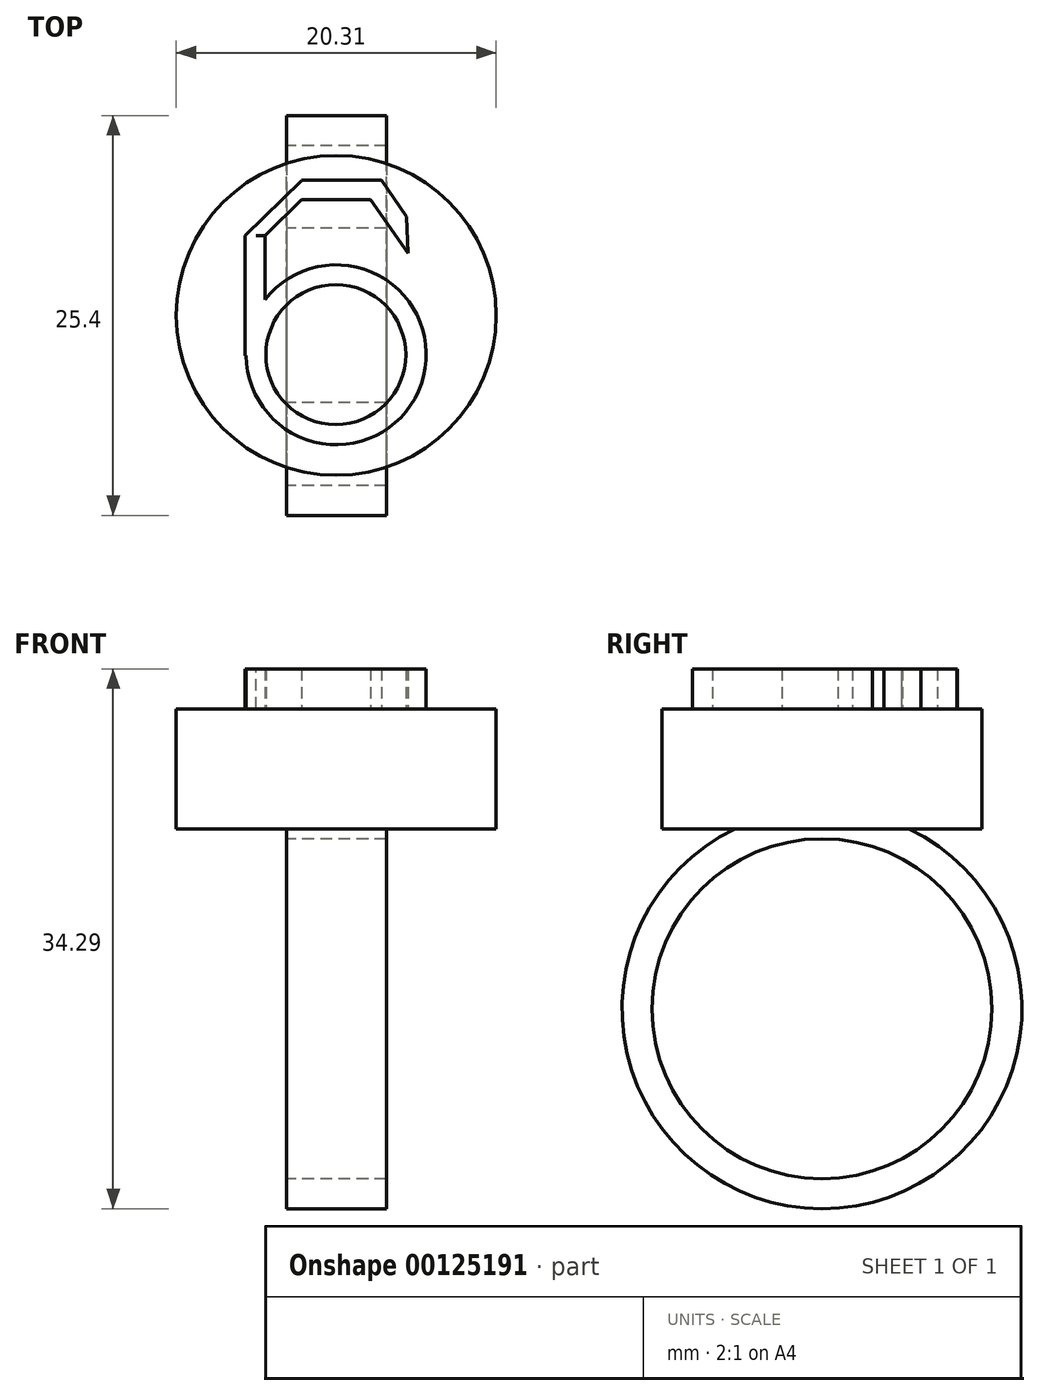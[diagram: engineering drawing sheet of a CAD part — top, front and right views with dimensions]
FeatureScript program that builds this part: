
annotation { "Feature Type Name" : "Feature", "Feature Type Description" : "" }
export const myFeature = defineFeature(function(context is Context, id is Id, definition is map)
    precondition{}
    {
        {
            var Q0;
            Q0=qCreatedBy(makeId("Right.planeOp"),FACE);
            var sketch = newSketch(context, id + "F0", { "sketchPlane" : qUnion([Q0])});
            skCircle(sketch, "E0", {"center": v(0, 0) * mm, "radius": 12.7 * mm});
            skSolve(sketch);
        }
        {
            var Q0;
            Q0 = qSketchRegion(id + "F0", true);
            extrude(context, id + "F1", {"entities" : qUnion([Q0]), "depth" : 6.35 * mm});
        }
        {
            var Q0;
            Q0=qCreatedBy(makeId("Right.planeOp"),FACE);
            var sketch = newSketch(context, id + "F2", { "sketchPlane" : qUnion([Q0])});
            skCircle(sketch, "E1", {"center": v(0, 0) * mm, "radius": 10.8 * mm});
            skSolve(sketch);
        }
        {
            var Q0;
            Q0 = qSketchRegion(id + "F2", true);
            extrude(context, id + "F3", {"entities" : qUnion([Q0]), "operationType" : NewBodyOperationType.REMOVE, "depth" : 55.84 * mm});
        }
        {
            var Q0;
            Q0=qCreatedBy(makeId("Top.planeOp"),FACE);
            cPlane(context, id + "F4", {"entities" : qUnion([Q0]), "cplaneType" : CPlaneType.OFFSET, "offset" : 12.7 * mm, "width" : 152.4 * mm, "height" : 152.4 * mm});
        }
        {
            var Q0;
            Q0=qCreatedBy(id+"F4.planeOp",FACE);
            cPlane(context, id + "F5", {"entities" : qUnion([Q0]), "cplaneType" : CPlaneType.OFFSET, "offset" : 1.27 * mm, "oppositeDirection" : true, "width" : 152.4 * mm, "height" : 152.4 * mm});
        }
        {
            var Q0;
            Q0=qCreatedBy(id+"F5.planeOp",FACE);
            var sketch = newSketch(context, id + "F6", { "sketchPlane" : qUnion([Q0])});
            skCircle(sketch, "E2", {"center": v(3.16, 0) * mm, "radius": 10.16 * mm});
            skSolve(sketch);
        }
        {
            var Q0;
            Q0 = qSketchRegion(id + "F6", true);
            extrude(context, id + "F7", {"entities" : qUnion([Q0]), "operationType" : NewBodyOperationType.ADD, "depth" : 7.62 * mm});
        }
        {
            var Q0;
            Q0=qCreatedBy(id+"F5.planeOp",FACE);
            cPlane(context, id + "F8", {"entities" : qUnion([Q0]), "cplaneType" : CPlaneType.OFFSET, "offset" : 7.62 * mm, "width" : 152.4 * mm, "height" : 152.4 * mm});
        }
        {
            var Q0;
            Q0=qCreatedBy(id+"F8.planeOp",FACE);
            var sketch = newSketch(context, id + "F9", { "sketchPlane" : qUnion([Q0])});
            skCircle(sketch, "E3", {"center": v(3.16, -2.5) * mm, "radius": 5.72 * mm});
            skSolve(sketch);
        }
        {
            var Q0;
            Q0 = qSketchRegion(id + "F9", true);
            extrude(context, id + "F10", {"entities" : qUnion([Q0]), "operationType" : NewBodyOperationType.ADD, "depth" : 2.54 * mm});
        }
        {
            var Q0;
            Q0=qCreatedBy(id+"F8.planeOp",FACE);
            var sketch = newSketch(context, id + "F11", { "sketchPlane" : qUnion([Q0])});
            skCircle(sketch, "E4", {"center": v(3.13, -2.5) * mm, "radius": 4.45 * mm});
            skSolve(sketch);
        }
        {
            var Q0;
            Q0 = qSketchRegion(id + "F11", true);
            extrude(context, id + "F12", {"entities" : qUnion([Q0]), "operationType" : NewBodyOperationType.REMOVE, "depth" : 25.4 * mm});
        }
        {
            var Q0;
            Q0=qCreatedBy(id+"F8.planeOp",FACE);
            var sketch = newSketch(context, id + "F13", { "sketchPlane" : qUnion([Q0])});
            skLineSegment(sketch, "E5.bottom", {"start": v(-2.62, -2.54) * mm, "end": v(-1.35, -2.54) * mm});
            skLineSegment(sketch, "E5.top", {"start": v(-2.62, 5.08) * mm, "end": v(-1.35, 5.08) * mm});
            skLineSegment(sketch, "E5.left", {"start": v(-2.62, -2.54) * mm, "end": v(-2.62, 5.08) * mm});
            skLineSegment(sketch, "E5.right", {"start": v(-1.35, -2.54) * mm, "end": v(-1.35, 5.08) * mm});
            skSolve(sketch);
        }
        {
            var Q0;
            Q0 = qSketchRegion(id + "F13", true);
            extrude(context, id + "F14", {"entities" : qUnion([Q0]), "operationType" : NewBodyOperationType.ADD, "depth" : 2.54 * mm});
        }
        {
            var Q0;
            Q0=qCreatedBy(id+"F8.planeOp",FACE);
            var sketch = newSketch(context, id + "F15", { "sketchPlane" : qUnion([Q0])});
            skLineSegment(sketch, "E6", {"start": v(-2.65, 5.05) * mm, "end": v(1, 8.6) * mm});
            skLineSegment(sketch, "E7", {"start": v(-1.34, 5.1) * mm, "end": v(2.25, 8.6) * mm});
            skLineSegment(sketch, "E8", {"start": v(1, 8.6) * mm, "end": v(2.25, 8.6) * mm});
            skLineSegment(sketch, "E9", {"start": v(-2.65, 5.05) * mm, "end": v(-1.34, 5.1) * mm});
            skSolve(sketch);
        }
        {
            var Q0;
            Q0 = qSketchRegion(id + "F15", true);
            extrude(context, id + "F16", {"entities" : qUnion([Q0]), "operationType" : NewBodyOperationType.ADD, "depth" : 2.54 * mm});
        }
        {
            var Q0;
            Q0=qCreatedBy(id+"F8.planeOp",FACE);
            var sketch = newSketch(context, id + "F17", { "sketchPlane" : qUnion([Q0])});
            skLineSegment(sketch, "E10", {"start": v(0.95, 8.6) * mm, "end": v(0.95, 7.34) * mm});
            skLineSegment(sketch, "E11", {"start": v(0.95, 7.34) * mm, "end": v(6.02, 7.34) * mm});
            skLineSegment(sketch, "E12", {"start": v(6.02, 7.34) * mm, "end": v(6.02, 8.6) * mm});
            skLineSegment(sketch, "E13", {"start": v(6.02, 8.6) * mm, "end": v(0.95, 8.6) * mm});
            skSolve(sketch);
        }
        {
            var Q0;
            Q0 = qSketchRegion(id + "F17", true);
            extrude(context, id + "F18", {"entities" : qUnion([Q0]), "operationType" : NewBodyOperationType.ADD, "depth" : 2.54 * mm});
        }
        {
            var Q0;
            Q0=qCreatedBy(id+"F8.planeOp",FACE);
            var sketch = newSketch(context, id + "F19", { "sketchPlane" : qUnion([Q0])});
            skLineSegment(sketch, "E14", {"start": v(5.28, 7.43) * mm, "end": v(7.72, 3.95) * mm});
            skLineSegment(sketch, "E15", {"start": v(6.02, 8.58) * mm, "end": v(7.63, 6.29) * mm});
            skLineSegment(sketch, "E16", {"start": v(7.63, 6.29) * mm, "end": v(7.72, 3.95) * mm});
            skLineSegment(sketch, "E17", {"start": v(6.02, 8.58) * mm, "end": v(5.28, 7.43) * mm});
            skSolve(sketch);
        }
        {
            var Q0;
            Q0 = qSketchRegion(id + "F19", true);
            extrude(context, id + "F20", {"entities" : qUnion([Q0]), "operationType" : NewBodyOperationType.ADD, "depth" : 2.54 * mm});
        }
    });
